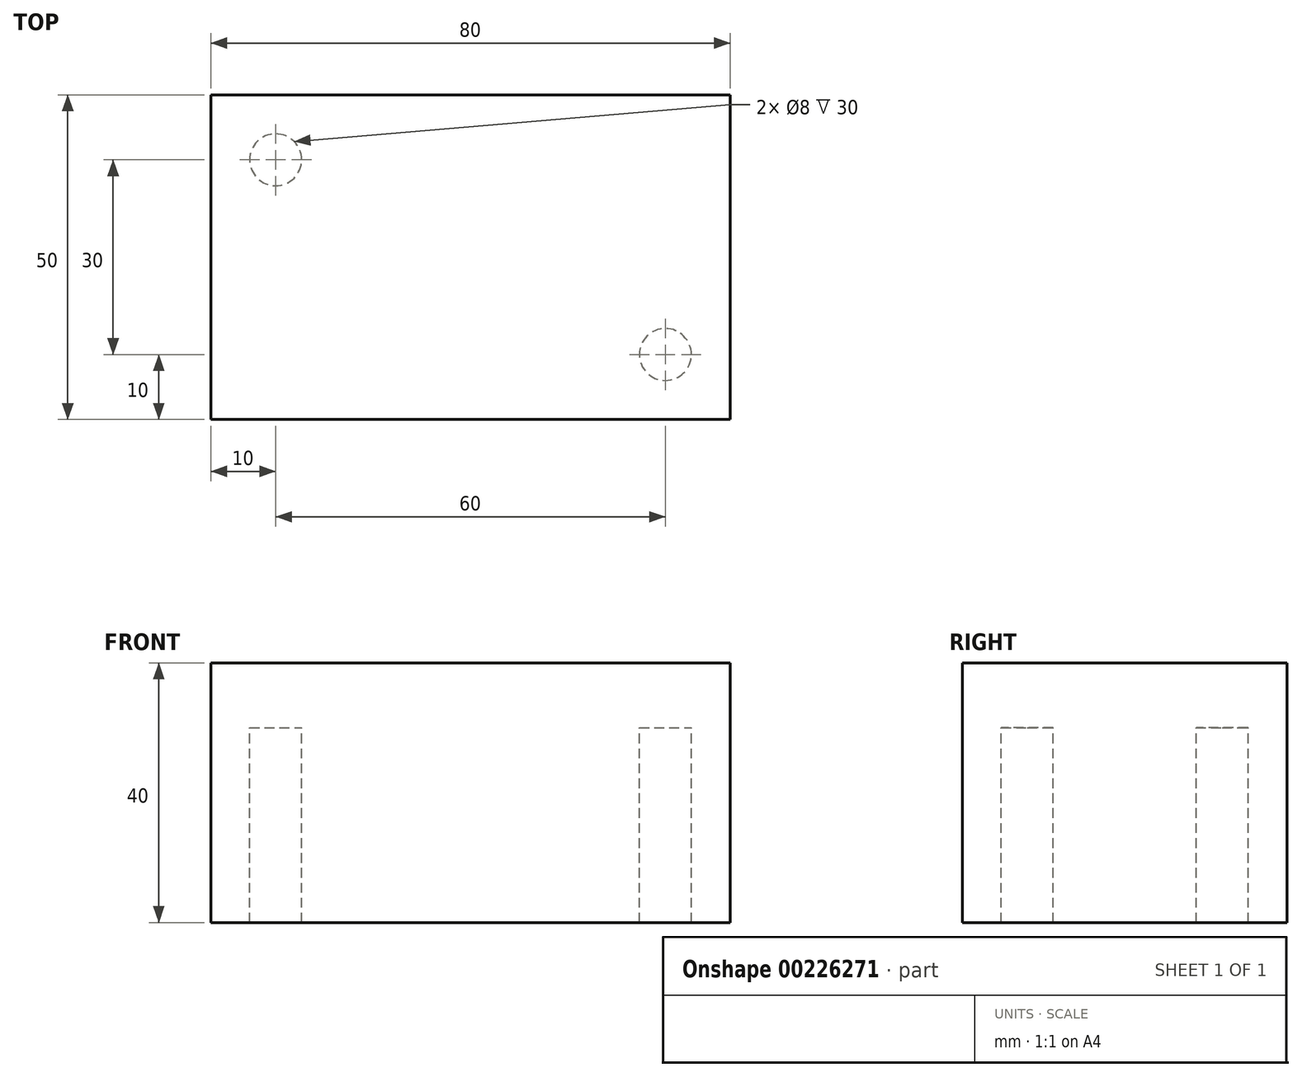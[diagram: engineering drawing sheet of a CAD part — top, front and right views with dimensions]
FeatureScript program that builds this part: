
annotation { "Feature Type Name" : "Feature", "Feature Type Description" : "" }
export const myFeature = defineFeature(function(context is Context, id is Id, definition is map)
    precondition{}
    {
        {
            var Q0;
            Q0=qCreatedBy(makeId("Top.planeOp"),FACE);
            var sketch = newSketch(context, id + "F0", { "sketchPlane" : qUnion([Q0])});
            skLineSegment(sketch, "E0.bottom", {"start": v(40, 25) * mm, "end": v(-40, 25) * mm});
            skLineSegment(sketch, "E0.top", {"start": v(40, -25) * mm, "end": v(-40, -25) * mm});
            skLineSegment(sketch, "E0.left", {"start": v(40, 25) * mm, "end": v(40, -25) * mm});
            skLineSegment(sketch, "E0.right", {"start": v(-40, 25) * mm, "end": v(-40, -25) * mm});
            skPoint(sketch, "E0.middle", {"position": v(0, 0) * mm});
            skSolve(sketch);
        }
        {
            var Q0;
            Q0=makeQuery(id+"F0.imprint","IMPRINT",FACE,{"disambiguationData":[TD([[makeQuery(id+"F0.imprint","IMPRINT",EDGE,{"derivedFrom":sQuery(id+"F0.wireOp",EDGE,"E0.bottom")}),1.0]])]});
            extrude(context, id + "F1", {"entities" : qUnion([Q0]), "depth" : 10 * mm});
        }
        {
            var Q0;
            Q0=makeQuery(id+"F1.opExtrude","CAP_FACE",FACE,{"disambiguationData":[OSD([sQuery(id+"F0.wireOp",EDGE,"E0.bottom"),sQuery(id+"F0.wireOp",EDGE,"E0.top"),sQuery(id+"F0.wireOp",EDGE,"E0.left"),sQuery(id+"F0.wireOp",EDGE,"E0.right")])],"isStart":true});
            var sketch = newSketch(context, id + "F2", { "sketchPlane" : qUnion([Q0])});
            skCircle(sketch, "E1", {"center": v(-30, 15) * mm, "radius": 4 * mm});
            skCircle(sketch, "E2.MirrorC", {"center": v(30, 15) * mm, "radius": 4 * mm});
            skCircle(sketch, "E3.MirrorC", {"center": v(30, -15) * mm, "radius": 4 * mm});
            skCircle(sketch, "E4.MirrorC", {"center": v(-30, -15) * mm, "radius": 4 * mm});
            skSolve(sketch);
        }
        {
            var Q0;
            Q0=makeQuery(id+"F2.imprint","IMPRINT",FACE,{"disambiguationData":[TD([[makeQuery(id+"F2.imprint","IMPRINT",EDGE,{"derivedFrom":sQuery(id+"F2.wireOp",EDGE,"E1")}),1.0]])]});
            var Q1;
            Q1=makeQuery(id+"F2.imprint","IMPRINT",FACE,{"disambiguationData":[TD([[makeQuery(id+"F2.imprint","IMPRINT",EDGE,{"derivedFrom":sQuery(id+"F2.wireOp",EDGE,"E4.MirrorC")}),-1.0]])]});
            var Q2;
            Q2=makeQuery(id+"F2.imprint","IMPRINT",FACE,{"disambiguationData":[TD([[makeQuery(id+"F2.imprint","IMPRINT",EDGE,{"derivedFrom":sQuery(id+"F2.wireOp",EDGE,"E3.MirrorC")}),1.0]])]});
            var Q3;
            Q3=makeQuery(id+"F2.imprint","IMPRINT",FACE,{"disambiguationData":[TD([[makeQuery(id+"F2.imprint","IMPRINT",EDGE,{"derivedFrom":sQuery(id+"F2.wireOp",EDGE,"E2.MirrorC")}),-1.0]])]});
            extrude(context, id + "F3", {"entities" : qUnion([Q0, Q1, Q2, Q3]), "operationType" : NewBodyOperationType.ADD, "depth" : 30 * mm});
        }
    });
